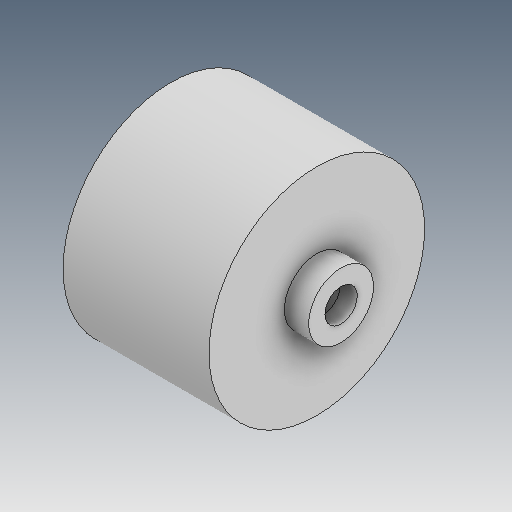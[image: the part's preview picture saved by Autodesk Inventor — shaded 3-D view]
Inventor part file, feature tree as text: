
AUTODESK INVENTOR PART (.ipt)
format: ipt  version: 2021 (Build 250183000, 183)  size: 138,752 bytes
history: native  units: in
note: dims shown in document units (in); Inventor stores cm internally (conversion verified against a paired STEP export)
features: sketch x6, extrude x3, other x2
ambient origin geometry x8: Origin, YZ Plane, XZ Plane, XY Plane, X Axis, Y Axis, Z Axis, Center Point
bodies: Body1 (feature_tree)
feature tree (11):
  other  "Sólido1"
  other  "Revolução1"
  extrude  "Extrusão1"  Depth=0.2618in
  extrude  "Extrusão2"  Depth=0.0984in
  sketch  "Esboço4"  dims[d6=0.0591in d7=0.0in]
  sketch  "Esboço5"  dims[d8=0.1181in]
  extrude  "Extrusão3"  Depth=0.1575in
  sketch  "Esboço1"  dims[d0=0.3543in d1=0.2618in]
  sketch  "Esboço2"  dims[d2=0.0787in d3=0.0984in]
  sketch  "Esboço3"  dims[d4=90.0deg d5=0.1575in]
  sketch  "Esboço6"  dims[d9=0.1575in d10=0.0in d11=0.0787in d12=0.0417in d13=0.0in]
